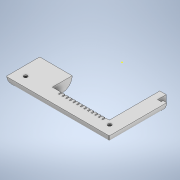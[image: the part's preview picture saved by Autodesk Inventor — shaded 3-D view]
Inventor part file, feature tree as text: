
AUTODESK INVENTOR PART (.ipt)
format: ipt  version: 2020 (Build 240168000, 168)  size: 1,036,288 bytes
history: native  units: mm
features: other x3, sketch x2, extrude x1
ambient origin geometry x8: Origin, YZ Plane, XZ Plane, XY Plane, X Axis, Y Axis, Z Axis, Center Point
bodies: Solid1 (feature_tree)
feature tree (6):
  other  "casing-backing.ipt"
  extrude  "Extrusion1"  Depth=10.0mm TaperAngle=0.0deg
  other  "Solid4::casing-backing.ipt"
  other  "TaggingFeature1"
  sketch  "Sketch1"  dims[d0=10.0mm d1=10.0mm d2=0.0mm]
  sketch  "Sketch6"  dims[d3=0.5mm d4=0.872665mm]
